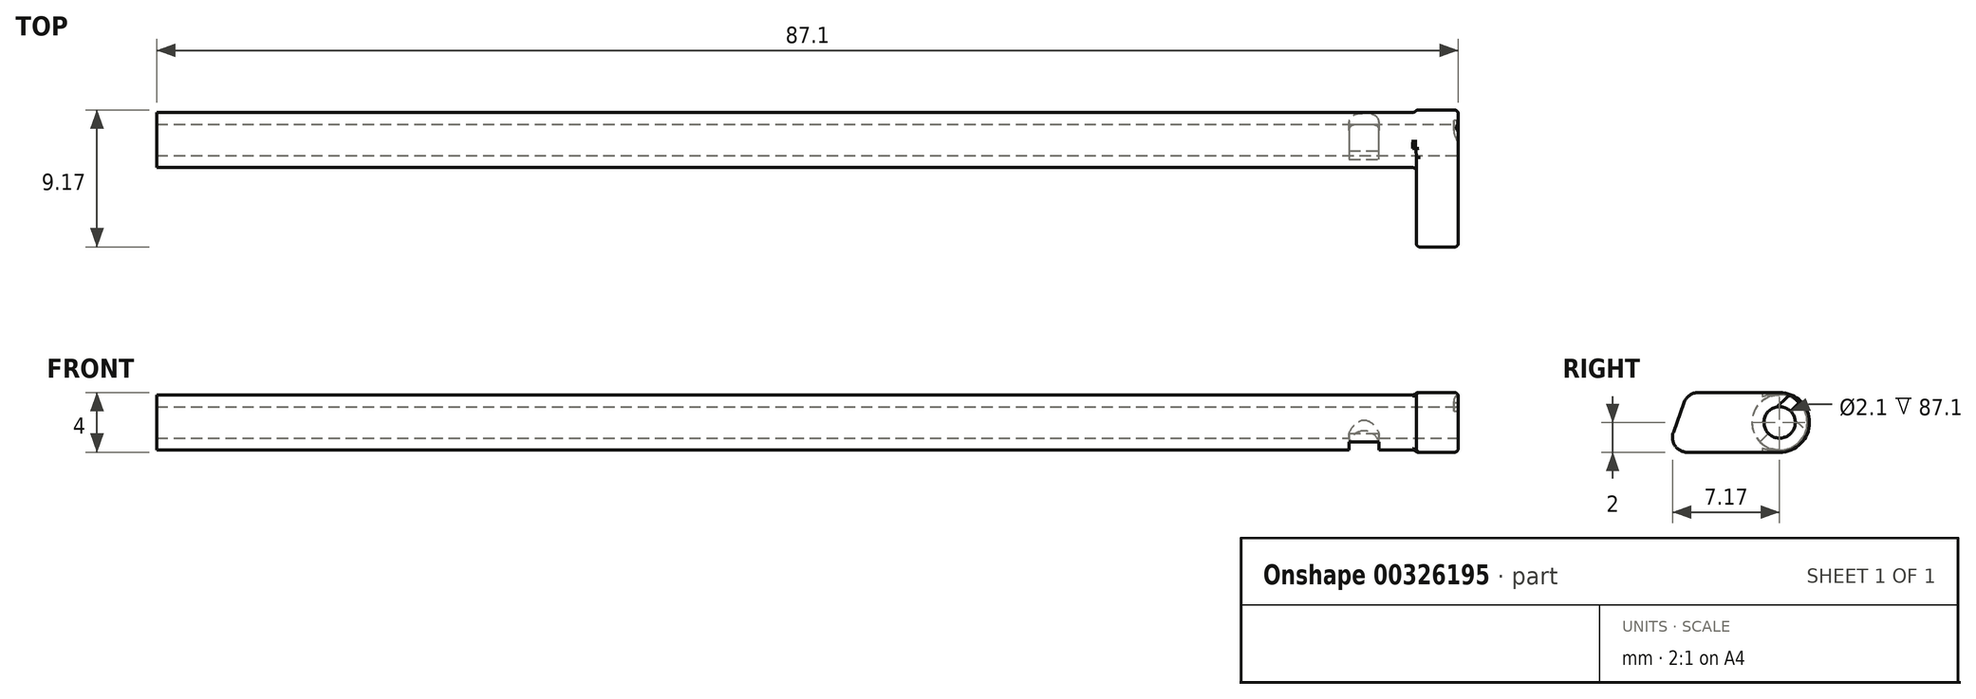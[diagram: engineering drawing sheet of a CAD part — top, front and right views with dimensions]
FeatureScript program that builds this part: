
annotation { "Feature Type Name" : "Feature", "Feature Type Description" : "" }
export const myFeature = defineFeature(function(context is Context, id is Id, definition is map)
    precondition{}
    {
        {
            var Q0;
            Q0=qCreatedBy(makeId("Right.planeOp"),FACE);
            var sketch = newSketch(context, id + "F0", { "sketchPlane" : qUnion([Q0])});
            skLineSegment(sketch, "E0", {"start": v(-1.6, -2) * mm, "end": v(-7.6, -2) * mm});
            skLineSegment(sketch, "E1", {"start": v(-7.6, -2) * mm, "end": v(-6.14, 2) * mm});
            skLineSegment(sketch, "E2", {"start": v(-6.14, 2) * mm, "end": v(-1.6, 2) * mm});
            skLineSegment(sketch, "E3", {"start": v(-1.6, 2) * mm, "end": v(-1.6, 0.7) * mm});
            skArc(sketch, "E4", {"start": v(0, 1.75) * mm, "mid": v(-1.75, 0) * mm, "end": v(0, -1.75) * mm});
            skLineSegment(sketch, "E5", {"start": v(-1.6, 0) * mm, "end": v(0, 0) * mm, "construction": true});
            skLineSegment(sketch, "E6", {"start": v(-1.6, 2) * mm, "end": v(0, 2) * mm});
            skLineSegment(sketch, "E7", {"start": v(0, 2) * mm, "end": v(0, 1.75) * mm});
            skLineSegment(sketch, "E8", {"start": v(0, -1.75) * mm, "end": v(0, -2) * mm});
            skLineSegment(sketch, "E9", {"start": v(0, -2) * mm, "end": v(-1.6, -2) * mm});
            skLineSegment(sketch, "E10.trimOffspring", {"start": v(-1.6, -0.7) * mm, "end": v(-1.6, -2) * mm});
            skLineSegment(sketch, "E11", {"start": v(-1.6, 0.7) * mm, "end": v(-1.6, -0.7) * mm});
            skSolve(sketch);
        }
        {
            var Q0;
            Q0=makeQuery(id+"F0.imprint","IMPRINT",FACE,{"disambiguationData":[TD([[makeQuery(id+"F0.imprint","IMPRINT",EDGE,{"derivedFrom":sQuery(id+"F0.wireOp",EDGE,"E0")}),-1.0]])]});
            var Q1;
            {var subQ0=sQuery(id+"F0.wireOp",EDGE,"E3");Q1=makeQuery(id+"F0.imprint","IMPRINT",FACE,{"disambiguationData":[TD([[makeQuery(id+"F0.imprint","IMPRINT",EDGE,{"derivedFrom":subQ0}),1.0]])]});}
            var Q2;
            {var subQ0=sQuery(id+"F0.wireOp",EDGE,"E8");Q2=makeQuery(id+"F0.imprint","IMPRINT",FACE,{"disambiguationData":[TD([[makeQuery(id+"F0.imprint","IMPRINT",EDGE,{"derivedFrom":subQ0}),-1.0]])]});}
            var Q3;
            {var subQ0=sQuery(id+"F0.wireOp",EDGE,"E11");Q3=makeQuery(id+"F0.imprint","IMPRINT",FACE,{"disambiguationData":[TD([[makeQuery(id+"F0.imprint","IMPRINT",EDGE,{"derivedFrom":subQ0}),-1.0]])]});}
            extrude(context, id + "F1", {"entities" : qUnion([Q0, Q1, Q2, Q3]), "depth" : 2.8 * mm});
        }
        {
            var Q0;
            Q0=makeQuery(id+"F1.opExtrude","CAP_FACE",FACE,{"disambiguationData":[OSD([sQuery(id+"F0.wireOp",EDGE,"E0"),sQuery(id+"F0.wireOp",EDGE,"E1"),sQuery(id+"F0.wireOp",EDGE,"E2"),sQuery(id+"F0.wireOp",EDGE,"E4"),sQuery(id+"F0.wireOp",EDGE,"E6"),sQuery(id+"F0.wireOp",EDGE,"E7"),sQuery(id+"F0.wireOp",EDGE,"E8"),sQuery(id+"F0.wireOp",EDGE,"E9"),sQuery(id+"F0.wireOp",EDGE,"E11")])],"isStart":false});
            var sketch = newSketch(context, id + "F2", { "sketchPlane" : qUnion([Q0])});
            skCircle(sketch, "E12", {"center": v(0, 0) * mm, "radius": 1.85 * mm});
            skCircle(sketch, "E13", {"center": v(0, 0) * mm, "radius": 1.05 * mm});
            skCircle(sketch, "E14", {"center": v(0, 0) * mm, "radius": 2 * mm});
            skSolve(sketch);
        }
        {
            var Q0;
            Q0=makeQuery(id+"F2.imprint","IMPRINT",FACE,{"disambiguationData":[TD([[makeQuery(id+"F2.imprint","IMPRINT",EDGE,{"derivedFrom":sQuery(id+"F2.wireOp",EDGE,"E13")}),-1.0]])]});
            var Q1;
            {var subQ2=sQuery(id+"F0.wireOp",EDGE,"E11");Q1=makeQuery(id+"F2.imprint","IMPRINT",FACE,{"disambiguationData":[TD([[makeQuery(id+"F2.imprint","IMPRINT",EDGE,{"derivedFrom":makeQuery(id+"F1.opExtrude","CAP_EDGE",EDGE,{"disambiguationData":[OSD([subQ2])],"isStart":false})}),-1.0]])]});}
            var Q2;
            {var subQ0=sQuery(id+"F2.wireOp",EDGE,"E12");var subQ1=makeQuery(id+"F1.opExtrude","CAP_EDGE",EDGE,{"disambiguationData":[OSD([sQuery(id+"F0.wireOp",EDGE,"E7")])],"isStart":false});var subQ2=makeQuery(id+"F2.imprint","INTERSECT",VERTEX,{"derivedFrom":[subQ1,subQ0]});Q2=makeQuery(id+"F2.imprint","IMPRINT",FACE,{"disambiguationData":[TD([[makeQuery(id+"F2.imprint","IMPRINT",EDGE,{"disambiguationData":[TD([[subQ2,1.0]])],"derivedFrom":subQ0}),-1.0]])]});}
            var Q3;
            Q3=makeQuery(id+"F1.opExtrude","CAP_FACE",FACE,{"disambiguationData":[OSD([sQuery(id+"F0.wireOp",EDGE,"E0"),sQuery(id+"F0.wireOp",EDGE,"E1"),sQuery(id+"F0.wireOp",EDGE,"E2"),sQuery(id+"F0.wireOp",EDGE,"E4"),sQuery(id+"F0.wireOp",EDGE,"E6"),sQuery(id+"F0.wireOp",EDGE,"E7"),sQuery(id+"F0.wireOp",EDGE,"E8"),sQuery(id+"F0.wireOp",EDGE,"E9"),sQuery(id+"F0.wireOp",EDGE,"E11")])],"isStart":true});
            extrude(context, id + "F3", {"entities" : qUnion([Q0, Q1, Q2]), "operationType" : NewBodyOperationType.ADD, "endBound" : BoundingType.UP_TO_SURFACE, "oppositeDirection" : true, "endBoundEntityFace" : qUnion([Q3]), "depth" : 25 * mm});
        }
        {
            var Q0;
            Q0=makeQuery(id+"F2.imprint","IMPRINT",FACE,{"disambiguationData":[TD([[makeQuery(id+"F2.imprint","IMPRINT",EDGE,{"derivedFrom":sQuery(id+"F2.wireOp",EDGE,"E13")}),-1.0]])]});
            var Q1;
            {var subQ2=sQuery(id+"F0.wireOp",EDGE,"E11");Q1=makeQuery(id+"F2.imprint","IMPRINT",FACE,{"disambiguationData":[TD([[makeQuery(id+"F2.imprint","IMPRINT",EDGE,{"derivedFrom":makeQuery(id+"F1.opExtrude","CAP_EDGE",EDGE,{"disambiguationData":[OSD([subQ2])],"isStart":false})}),-1.0]])]});}
            extrude(context, id + "F4", {"entities" : qUnion([Q0, Q1]), "operationType" : NewBodyOperationType.ADD, "oppositeDirection" : true, "depth" : 87.1 * mm});
        }
        {
            var Q0;
            {var subQ0=sQuery(id+"F0.wireOp",EDGE,"E11");var subQ1=sQuery(id+"F0.wireOp",EDGE,"E9");var subQ2=sQuery(id+"F0.wireOp",EDGE,"E8");var subQ3=sQuery(id+"F0.wireOp",EDGE,"E7");var subQ4=sQuery(id+"F0.wireOp",EDGE,"E6");var subQ5=sQuery(id+"F0.wireOp",EDGE,"E4");var subQ6=sQuery(id+"F0.wireOp",EDGE,"E2");var subQ7=sQuery(id+"F0.wireOp",EDGE,"E1");var subQ8=sQuery(id+"F0.wireOp",EDGE,"E0");Q0=makeQuery(id+"F4.boolean.opBoolean","INTERSECT",EDGE,{"derivedFrom":[makeQuery(id+"F3.boolean.opBoolean","MERGE",FACE,{"derivedFrom":[makeQuery(id+"F1.opExtrude","CAP_FACE",FACE,{"disambiguationData":[OSD([subQ8,subQ7,subQ6,subQ5,subQ4,subQ3,subQ2,subQ1,subQ0])],"isStart":true}),makeQuery(id+"F3.opExtrude","CAP_FACE",FACE,{"disambiguationData":[OSD([subQ8,subQ7,subQ6,subQ5,subQ4,subQ3,subQ2,subQ1,subQ0])],"isStart":false})]}),makeQuery(id+"F4.opExtrude","SWEPT_FACE",FACE,{"disambiguationData":[OSD([sQuery(id+"F2.wireOp",EDGE,"E12")])]})]});}
            fillet(context, id + "F5", {"entities" : qUnion([Q0]), "radius" : 0.25 * mm, "tangentPropagation" : true, "allowEdgeOverflow" : false});
        }
        {
            var Q0;
            Q0=makeQuery(id+"F1.opExtrude","CAP_EDGE",EDGE,{"disambiguationData":[OSD([sQuery(id+"F0.wireOp",EDGE,"E2"),sQuery(id+"F0.wireOp",EDGE,"E6")])],"isStart":false});
            var Q1;
            Q1=makeQuery(id+"F1.opExtrude","CAP_EDGE",EDGE,{"disambiguationData":[OSD([sQuery(id+"F0.wireOp",EDGE,"E0"),sQuery(id+"F0.wireOp",EDGE,"E9")])],"isStart":false});
            var Q2;
            Q2=makeQuery(id+"F1.opExtrude","CAP_EDGE",EDGE,{"disambiguationData":[OSD([sQuery(id+"F0.wireOp",EDGE,"E1")])],"isStart":false});
            var Q3;
            Q3=makeQuery(id+"F1.opExtrude","CAP_EDGE",EDGE,{"disambiguationData":[OSD([sQuery(id+"F0.wireOp",EDGE,"E2"),sQuery(id+"F0.wireOp",EDGE,"E6")])],"isStart":true});
            var Q4;
            Q4=makeQuery(id+"F1.opExtrude","CAP_EDGE",EDGE,{"disambiguationData":[OSD([sQuery(id+"F0.wireOp",EDGE,"E1")])],"isStart":true});
            var Q5;
            Q5=makeQuery(id+"F1.opExtrude","CAP_EDGE",EDGE,{"disambiguationData":[OSD([sQuery(id+"F0.wireOp",EDGE,"E0"),sQuery(id+"F0.wireOp",EDGE,"E9")])],"isStart":true});
            fillet(context, id + "F6", {"entities" : qUnion([Q0, Q1, Q2, Q3, Q4, Q5]), "radius" : 0.25 * mm, "tangentPropagation" : true, "allowEdgeOverflow" : false});
        }
        {
            var Q0;
            Q0=makeQuery(id+"F1.opExtrude","SWEPT_EDGE",EDGE,{"disambiguationData":[OSD([sQuery(id+"F0.wireOp",EDGE,"E1"),sQuery(id+"F0.wireOp",EDGE,"E2")])]});
            var Q1;
            Q1=makeQuery(id+"F1.opExtrude","SWEPT_EDGE",EDGE,{"disambiguationData":[OSD([sQuery(id+"F0.wireOp",EDGE,"E0"),sQuery(id+"F0.wireOp",EDGE,"E1")])]});
            fillet(context, id + "F7", {"entities" : qUnion([Q0, Q1]), "radius" : 1 * mm, "tangentPropagation" : true, "allowEdgeOverflow" : false});
        }
        {
            var Q0;
            Q0=qCreatedBy(makeId("Front.planeOp"),FACE);
            var sketch = newSketch(context, id + "F8", { "sketchPlane" : qUnion([Q0])});
            skLineSegment(sketch, "E15", {"start": v(-4.5, 0) * mm, "end": v(-4.5, -3) * mm});
            skLineSegment(sketch, "E16", {"start": v(-4.5, -3) * mm, "end": v(-2.5, -3) * mm});
            skLineSegment(sketch, "E17", {"start": v(-2.5, -3) * mm, "end": v(-2.5, 0) * mm});
            skLineSegment(sketch, "E18", {"start": v(-2.5, 0) * mm, "end": v(-4.5, 0) * mm});
            skLineSegment(sketch, "E19", {"start": v(-84.3, 0) * mm, "end": v(-4.5, 0) * mm, "construction": true});
            skSolve(sketch);
        }
        {
            var Q0;
            Q0=makeQuery(id+"F8.imprint","IMPRINT",FACE,{"disambiguationData":[TD([[makeQuery(id+"F8.imprint","IMPRINT",EDGE,{"derivedFrom":sQuery(id+"F8.wireOp",EDGE,"E15")}),1.0]])]});
            var Q1;
            Q1=sQuery(id+"F8.wireOp",EDGE,"E19");
            revolve(context, id + "F9", {"operationType" : NewBodyOperationType.REMOVE, "entities" : qUnion([Q0]), "axis" : qUnion([Q1]), "revolveType" : RevolveType.SYMMETRIC, "angle" : 90 * degree});
        }
        {
            var Q0;
            Q0=makeQuery(id+"F9.boolean.opBoolean","COPY",FACE,{"derivedFrom":makeQuery(id+"F9.opRevolve","CAP_FACE",FACE,{"disambiguationData":[OSD([sQuery(id+"F8.wireOp",EDGE,"E15"),sQuery(id+"F8.wireOp",EDGE,"E16"),sQuery(id+"F8.wireOp",EDGE,"E17"),sQuery(id+"F8.wireOp",EDGE,"E18")])],"isStart":false})});
            var sketch = newSketch(context, id + "F10", { "sketchPlane" : qUnion([Q0])});
            skLineSegment(sketch, "E20.bottom", {"start": v(-4.5, -1.85) * mm, "end": v(-2.5, -1.85) * mm});
            skLineSegment(sketch, "E20.top", {"start": v(-4.5, 0) * mm, "end": v(-2.5, 0) * mm});
            skLineSegment(sketch, "E20.left", {"start": v(-4.5, -1.85) * mm, "end": v(-4.5, 0) * mm});
            skLineSegment(sketch, "E20.right", {"start": v(-2.5, -1.85) * mm, "end": v(-2.5, 0) * mm});
            skSolve(sketch);
        }
        {
            var Q0;
            Q0=makeQuery(id+"F9.boolean.opBoolean","COPY",FACE,{"derivedFrom":makeQuery(id+"F9.opRevolve","CAP_FACE",FACE,{"disambiguationData":[OSD([sQuery(id+"F8.wireOp",EDGE,"E15"),sQuery(id+"F8.wireOp",EDGE,"E16"),sQuery(id+"F8.wireOp",EDGE,"E17"),sQuery(id+"F8.wireOp",EDGE,"E18")])],"isStart":true})});
            var sketch = newSketch(context, id + "F11", { "sketchPlane" : qUnion([Q0])});
            skLineSegment(sketch, "E21.bottom", {"start": v(-4.5, 1.85) * mm, "end": v(-2.5, 1.85) * mm});
            skLineSegment(sketch, "E21.top", {"start": v(-4.5, 0) * mm, "end": v(-2.5, 0) * mm});
            skLineSegment(sketch, "E21.left", {"start": v(-4.5, 1.85) * mm, "end": v(-4.5, 0) * mm});
            skLineSegment(sketch, "E21.right", {"start": v(-2.5, 1.85) * mm, "end": v(-2.5, 0) * mm});
            skSolve(sketch);
        }
        {
            var Q0;
            Q0 = qSketchRegion(id + "F10", true);
            extrude(context, id + "F12", {"entities" : qUnion([Q0]), "operationType" : NewBodyOperationType.REMOVE, "oppositeDirection" : true, "depth" : 0.85 * mm});
        }
        {
            var Q0;
            Q0 = qSketchRegion(id + "F11", true);
            extrude(context, id + "F13", {"entities" : qUnion([Q0]), "operationType" : NewBodyOperationType.REMOVE, "oppositeDirection" : true, "depth" : 0.85 * mm});
        }
        {
            var Q0;
            Q0=makeQuery(id+"F13.boolean.opBoolean","COPY",EDGE,{"derivedFrom":makeQuery(id+"F13.opExtrude","CAP_EDGE",EDGE,{"disambiguationData":[OSD([sQuery(id+"F11.wireOp",EDGE,"E21.right")])],"isStart":false})});
            var Q1;
            Q1=makeQuery(id+"F13.boolean.opBoolean","COPY",EDGE,{"derivedFrom":makeQuery(id+"F13.opExtrude","CAP_EDGE",EDGE,{"disambiguationData":[OSD([sQuery(id+"F11.wireOp",EDGE,"E21.left")])],"isStart":false})});
            var Q2;
            Q2=makeQuery(id+"F12.boolean.opBoolean","COPY",EDGE,{"derivedFrom":makeQuery(id+"F12.opExtrude","CAP_EDGE",EDGE,{"disambiguationData":[OSD([sQuery(id+"F10.wireOp",EDGE,"E20.left")])],"isStart":false})});
            var Q3;
            Q3=makeQuery(id+"F12.boolean.opBoolean","COPY",EDGE,{"derivedFrom":makeQuery(id+"F12.opExtrude","CAP_EDGE",EDGE,{"disambiguationData":[OSD([sQuery(id+"F10.wireOp",EDGE,"E20.right")])],"isStart":false})});
            fillet(context, id + "F14", {"entities" : qUnion([Q0, Q1, Q2, Q3]), "radius" : 1 * mm, "tangentPropagation" : true, "allowEdgeOverflow" : false});
        }
    });
